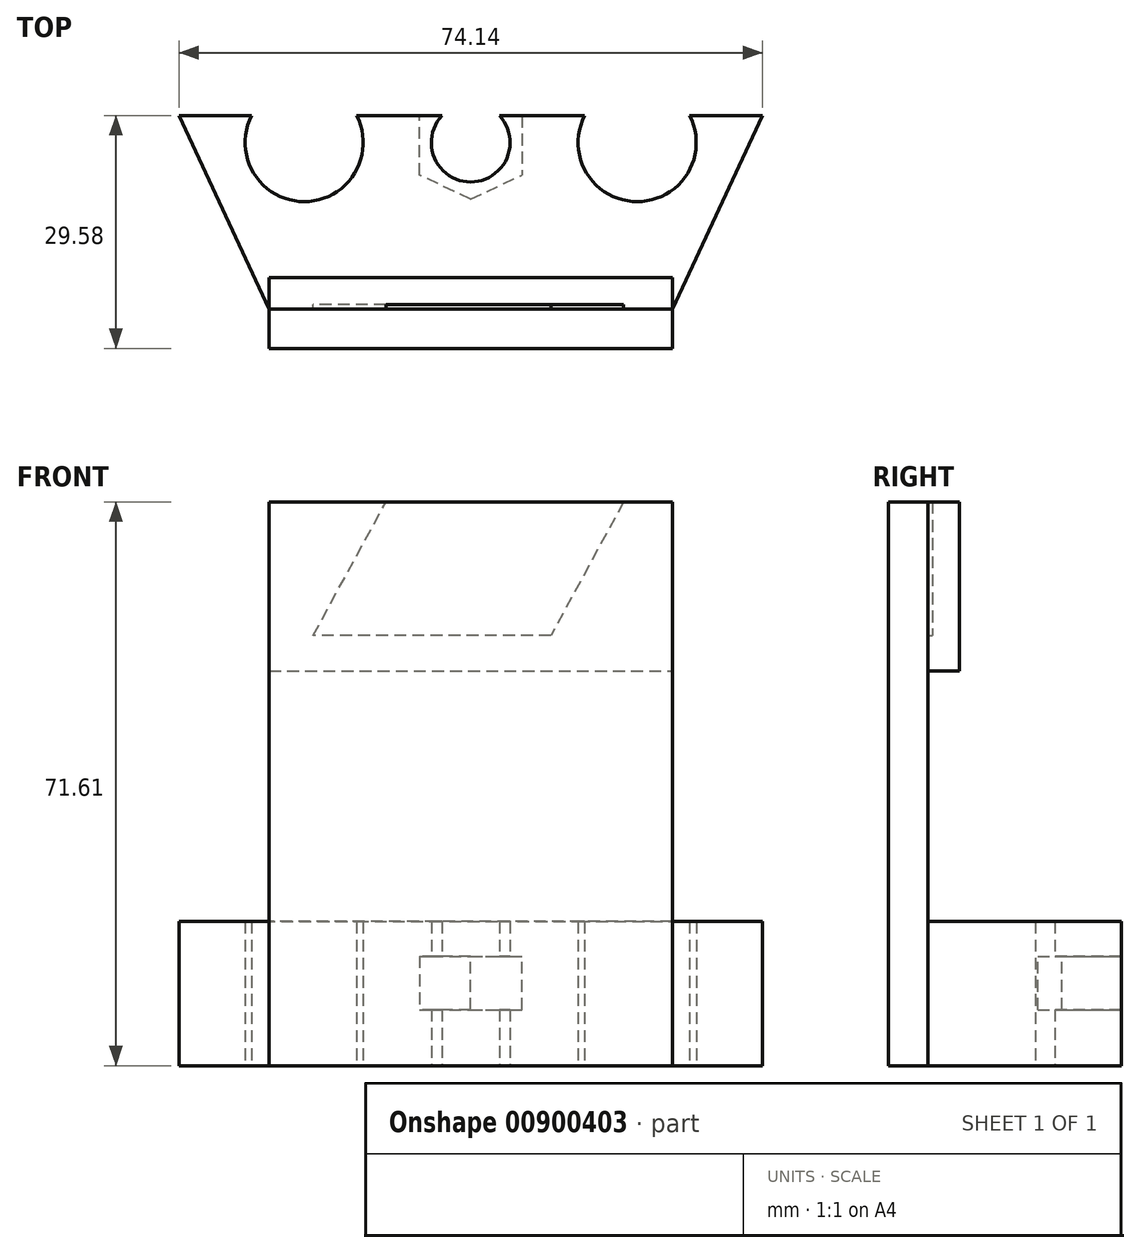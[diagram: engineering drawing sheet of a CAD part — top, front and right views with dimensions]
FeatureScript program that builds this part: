
annotation { "Feature Type Name" : "Feature", "Feature Type Description" : "" }
export const myFeature = defineFeature(function(context is Context, id is Id, definition is map)
    precondition{}
    {
        {
            var Q0;
            Q0=qCreatedBy(makeId("Top.planeOp"),FACE);
            var sketch = newSketch(context, id + "F0", { "sketchPlane" : qUnion([Q0])});
            skPoint(sketch, "E0.middle", {"position": v(0, 0) * mm});
            skCircle(sketch, "E1", {"center": v(21.15, 0) * mm, "radius": 7.5 * mm});
            skCircle(sketch, "E2", {"center": v(-21.15, 0) * mm, "radius": 7.5 * mm});
            skLineSegment(sketch, "E3", {"start": v(-6.5, 0) * mm, "end": v(-6.5, 4.12) * mm});
            skLineSegment(sketch, "E4", {"start": v(-6.5, 0) * mm, "end": v(-6.5, -4.12) * mm});
            skLineSegment(sketch, "E5", {"start": v(6.5, 0) * mm, "end": v(6.5, 4.12) * mm});
            skLineSegment(sketch, "E6", {"start": v(6.5, 0) * mm, "end": v(6.5, -4.12) * mm});
            skLineSegment(sketch, "E7", {"start": v(0, 7.2) * mm, "end": v(-6.5, 4.12) * mm});
            skLineSegment(sketch, "E8", {"start": v(0, 7.2) * mm, "end": v(6.5, 4.12) * mm});
            skLineSegment(sketch, "E9", {"start": v(0, -7.2) * mm, "end": v(-6.5, -4.12) * mm});
            skLineSegment(sketch, "E10", {"start": v(0, -7.2) * mm, "end": v(6.5, -4.12) * mm});
            skSolve(sketch);
        }
        {
            var Q0;
            Q0=makeQuery(id+"F0.imprint","IMPRINT",FACE,{"disambiguationData":[TD([[makeQuery(id+"F0.imprint","IMPRINT",EDGE,{"derivedFrom":sQuery(id+"F0.wireOp",EDGE,"E2")}),1.0]])]});
            var Q1;
            Q1=makeQuery(id+"F0.imprint","IMPRINT",FACE,{"disambiguationData":[TD([[makeQuery(id+"F0.imprint","IMPRINT",EDGE,{"derivedFrom":sQuery(id+"F0.wireOp",EDGE,"E1")}),1.0]])]});
            extrude(context, id + "F1", {"entities" : qUnion([Q0, Q1]), "depth" : 7.6 * mm, "offsetDistance" : 25 * mm, "hasSecondDirection" : true, "secondDirectionOppositeDirection" : true, "secondDirectionDepth" : 17.3 * mm});
        }
        {
            var Q0;
            Q0=makeQuery(id+"F0.imprint","IMPRINT",FACE,{"disambiguationData":[TD([[makeQuery(id+"F0.imprint","IMPRINT",EDGE,{"derivedFrom":sQuery(id+"F0.wireOp",EDGE,"E3")}),-1.0]])]});
            extrude(context, id + "F2", {"entities" : qUnion([Q0]), "oppositeDirection" : true, "depth" : 6.8 * mm, "offsetDistance" : 25 * mm});
        }
        {
            var Q0;
            Q0=qCreatedBy(makeId("Top.planeOp"),FACE);
            var sketch = newSketch(context, id + "F3", { "sketchPlane" : qUnion([Q0])});
            skLineSegment(sketch, "E11.top", {"start": v(25.61, -21.15) * mm, "end": v(-25.61, -21.15) * mm});
            skPoint(sketch, "E11.middle", {"position": v(0, 0) * mm});
            skLineSegment(sketch, "E12", {"start": v(-37.07, 3.43) * mm, "end": v(37.07, 3.43) * mm});
            skPoint(sketch, "E13.orphan", {"position": v(-53, 21.15) * mm});
            skPoint(sketch, "E14.orphan", {"position": v(53, 21.15) * mm});
            skLineSegment(sketch, "E15", {"start": v(-37.07, 3.43) * mm, "end": v(-25.61, -21.15) * mm});
            skLineSegment(sketch, "E16", {"start": v(37.07, 3.43) * mm, "end": v(25.61, -21.15) * mm});
            skPoint(sketch, "E17.orphan", {"position": v(-53, -21.15) * mm});
            skPoint(sketch, "E11.left.end.orphan", {"position": v(53, -21.15) * mm});
            skSolve(sketch);
        }
        {
            var Q0;
            Q0 = qSketchRegion(id + "F3", true);
            extrude(context, id + "F4", {"entities" : qUnion([Q0]), "depth" : 4.4 * mm, "offsetDistance" : 25 * mm, "hasSecondDirection" : true, "secondDirectionOppositeDirection" : true, "secondDirectionDepth" : 13.9 * mm});
        }
        {
            var Q0;
            Q0=makeQuery(id+"F1.opExtrude","SWEPT_BODY",BODY,{"disambiguationData":[OSD([sQuery(id+"F0.wireOp",EDGE,"E2")])]});
            var Q1;
            Q1=makeQuery(id+"F2.opExtrude","SWEPT_BODY",BODY,{"disambiguationData":[OSD([sQuery(id+"F0.wireOp",EDGE,"E3"),sQuery(id+"F0.wireOp",EDGE,"E4"),sQuery(id+"F0.wireOp",EDGE,"E5"),sQuery(id+"F0.wireOp",EDGE,"E6"),sQuery(id+"F0.wireOp",EDGE,"E7"),sQuery(id+"F0.wireOp",EDGE,"E8"),sQuery(id+"F0.wireOp",EDGE,"E9"),sQuery(id+"F0.wireOp",EDGE,"E10")])]});
            var Q2;
            Q2=makeQuery(id+"F1.opExtrude","SWEPT_BODY",BODY,{"disambiguationData":[OSD([sQuery(id+"F0.wireOp",EDGE,"E1")])]});
            var Q3;
            Q3=makeQuery(id+"F4.opExtrude","SWEPT_BODY",BODY,{"disambiguationData":[OSD([sQuery(id+"F3.wireOp",EDGE,"E11.top"),sQuery(id+"F3.wireOp",EDGE,"E12"),sQuery(id+"F3.wireOp",EDGE,"E15"),sQuery(id+"F3.wireOp",EDGE,"E16")])]});
            booleanBodies(context, id + "F5", {"operationType" : BooleanOperationType.SUBTRACTION, "tools" : qUnion([Q0, Q1, Q2]), "targets" : qUnion([Q3])});
        }
        {
            var Q0;
            Q0=makeQuery(id+"F4.opExtrude","SWEPT_FACE",FACE,{"disambiguationData":[OSD([sQuery(id+"F3.wireOp",EDGE,"E11.top")])]});
            var sketch = newSketch(context, id + "F6", { "sketchPlane" : qUnion([Q0])});
            skLineSegment(sketch, "E18.bottom", {"start": v(25.61, -13.9) * mm, "end": v(-25.61, -13.9) * mm});
            skLineSegment(sketch, "E18.top", {"start": v(25.61, 57.71) * mm, "end": v(-25.61, 57.71) * mm});
            skLineSegment(sketch, "E18.left", {"start": v(25.61, -13.9) * mm, "end": v(25.61, 57.71) * mm});
            skLineSegment(sketch, "E18.right", {"start": v(-25.61, -13.9) * mm, "end": v(-25.61, 57.71) * mm});
            skSolve(sketch);
        }
        {
            var Q0;
            Q0 = qSketchRegion(id + "F6", true);
            extrude(context, id + "F7", {"entities" : qUnion([Q0]), "operationType" : NewBodyOperationType.ADD, "depth" : 5 * mm, "offsetDistance" : 25 * mm});
        }
        {
            var Q0;
            Q0=makeQuery(id+"F7.opExtrude","CAP_FACE",FACE,{"disambiguationData":[OSD([sQuery(id+"F6.wireOp",EDGE,"E18.bottom"),sQuery(id+"F6.wireOp",EDGE,"E18.top"),sQuery(id+"F6.wireOp",EDGE,"E18.left"),sQuery(id+"F6.wireOp",EDGE,"E18.right")])],"isStart":true});
            cPlane(context, id + "F8", {"entities" : qUnion([Q0]), "cplaneType" : CPlaneType.OFFSET, "offset" : 0.6 * mm, "width" : 150 * mm, "height" : 150 * mm});
        }
        {
            var Q0;
            Q0=qCreatedBy(id+"F8.planeOp",FACE);
            var sketch = newSketch(context, id + "F9", { "sketchPlane" : qUnion([Q0])});
            skPoint(sketch, "E19.middle", {"position": v(15.52, 42.84) * mm});
            skLineSegment(sketch, "E20.bottom", {"start": v(-20, 40.77) * mm, "end": v(20, 40.77) * mm});
            skLineSegment(sketch, "E20.top", {"start": v(-20, 58.77) * mm, "end": v(20, 58.77) * mm});
            skLineSegment(sketch, "E20.left", {"start": v(-20, 40.77) * mm, "end": v(-20, 58.77) * mm});
            skLineSegment(sketch, "E20.right", {"start": v(20, 40.77) * mm, "end": v(20, 58.77) * mm});
            skPoint(sketch, "E20.middle", {"position": v(0, 49.77) * mm});
            skLineSegment(sketch, "E21", {"start": v(20, 40.77) * mm, "end": v(10.2, 58.77) * mm});
            skLineSegment(sketch, "E22", {"start": v(-20, 58.77) * mm, "end": v(-10.2, 40.77) * mm});
            skSolve(sketch);
        }
        {
            var Q0;
            {var subQ0=sQuery(id+"F9.wireOp",EDGE,"E21");Q0=makeQuery(id+"F9.imprint","IMPRINT",FACE,{"disambiguationData":[TD([[makeQuery(id+"F9.imprint","IMPRINT",EDGE,{"derivedFrom":subQ0}),1.0]])]});}
            extrude(context, id + "F10", {"entities" : qUnion([Q0]), "oppositeDirection" : true, "depth" : 0.6 * mm, "offsetDistance" : 25 * mm});
        }
        {
            var Q0;
            Q0=makeQuery(id+"F7.opExtrude","CAP_FACE",FACE,{"disambiguationData":[OSD([sQuery(id+"F6.wireOp",EDGE,"E18.bottom"),sQuery(id+"F6.wireOp",EDGE,"E18.top"),sQuery(id+"F6.wireOp",EDGE,"E18.left"),sQuery(id+"F6.wireOp",EDGE,"E18.right")])],"isStart":true});
            var sketch = newSketch(context, id + "F11", { "sketchPlane" : qUnion([Q0])});
            skLineSegment(sketch, "E23.bottom", {"start": v(25.61, 57.71) * mm, "end": v(-25.61, 57.71) * mm});
            skLineSegment(sketch, "E23.top", {"start": v(25.61, 36.27) * mm, "end": v(-25.61, 36.27) * mm});
            skLineSegment(sketch, "E23.left", {"start": v(25.61, 57.71) * mm, "end": v(25.61, 36.27) * mm});
            skLineSegment(sketch, "E23.right", {"start": v(-25.61, 57.71) * mm, "end": v(-25.61, 36.27) * mm});
            skSolve(sketch);
        }
        {
            var Q0;
            Q0 = qSketchRegion(id + "F11", true);
            extrude(context, id + "F12", {"entities" : qUnion([Q0]), "depth" : 4 * mm, "offsetDistance" : 25 * mm});
        }
        {
            var Q0;
            Q0=makeQuery(id+"F10.opExtrude","SWEPT_BODY",BODY,{"disambiguationData":[OSD([sQuery(id+"F9.wireOp",EDGE,"E20.bottom"),sQuery(id+"F9.wireOp",EDGE,"E20.top"),sQuery(id+"F9.wireOp",EDGE,"fwrjMXQo-WK6m-b8dY-bK3l-eFTgvQqSunGT"),sQuery(id+"F9.wireOp",EDGE,"8jJp1skS-lJIg-1qho-8Ot2-DPL0oGVGmFII")])]});
            var Q1;
            Q1=makeQuery(id+"F12.opExtrude","SWEPT_BODY",BODY,{"disambiguationData":[OSD([sQuery(id+"F11.wireOp",EDGE,"E23.bottom"),sQuery(id+"F11.wireOp",EDGE,"E23.top"),sQuery(id+"F11.wireOp",EDGE,"E23.left"),sQuery(id+"F11.wireOp",EDGE,"E23.right")])]});
            booleanBodies(context, id + "F13", {"operationType" : BooleanOperationType.SUBTRACTION, "tools" : qUnion([Q0]), "targets" : qUnion([Q1])});
        }
        {
            var Q0;
            Q0=makeQuery(id+"F7.boolean.opBoolean","MERGE",FACE,{"derivedFrom":[makeQuery(id+"F4.opExtrude","CAP_FACE",FACE,{"disambiguationData":[OSD([sQuery(id+"F3.wireOp",EDGE,"E11.top"),sQuery(id+"F3.wireOp",EDGE,"E12"),sQuery(id+"F3.wireOp",EDGE,"E15"),sQuery(id+"F3.wireOp",EDGE,"E16")])],"isStart":true}),makeQuery(id+"F7.opExtrude","SWEPT_FACE",FACE,{"disambiguationData":[OSD([sQuery(id+"F6.wireOp",EDGE,"E18.bottom")])]})]});
            var sketch = newSketch(context, id + "F14", { "sketchPlane" : qUnion([Q0])});
            skLineSegment(sketch, "E24.0.0", {"start": v(-6.5, -3.43) * mm, "end": v(-6.5, 4.12) * mm});
            skLineSegment(sketch, "E24.0.1", {"start": v(-6.5, 4.12) * mm, "end": v(0, 7.2) * mm});
            skLineSegment(sketch, "E24.0.2", {"start": v(0, 7.2) * mm, "end": v(6.5, 4.12) * mm});
            skLineSegment(sketch, "E24.0.3", {"start": v(6.5, 4.12) * mm, "end": v(6.5, -3.43) * mm});
            skLineSegment(sketch, "E24.0.4", {"start": v(6.5, -3.43) * mm, "end": v(-6.5, -3.43) * mm});
            skLineSegment(sketch, "E25.bottom", {"start": v(-6.5, 4.12) * mm, "end": v(6.5, 4.12) * mm});
            skLineSegment(sketch, "E25.top", {"start": v(-6.5, -12.92) * mm, "end": v(6.5, -12.92) * mm});
            skLineSegment(sketch, "E25.left", {"start": v(-6.5, 4.12) * mm, "end": v(-6.5, -12.92) * mm});
            skLineSegment(sketch, "E25.right", {"start": v(6.5, 4.12) * mm, "end": v(6.5, -12.92) * mm});
            skSolve(sketch);
        }
        {
            var Q0;
            {var subQ9=sQuery(id+"F14.wireOp",EDGE,"E24.0.1");Q0=makeQuery(id+"F14.imprint","IMPRINT",FACE,{"disambiguationData":[TD([[makeQuery(id+"F14.imprint","IMPRINT",EDGE,{"derivedFrom":subQ9}),1.0]])]});}
            var sketch = newSketch(context, id + "F15", { "sketchPlane" : qUnion([Q0])});
            skCircle(sketch, "E26", {"center": v(0, 0) * mm, "radius": 5 * mm});
            skSolve(sketch);
        }
        {
            var Q0;
            Q0 = qSketchRegion(id + "F15", true);
            extrude(context, id + "F16", {"entities" : qUnion([Q0]), "operationType" : NewBodyOperationType.REMOVE, "oppositeDirection" : true, "depth" : 25 * mm, "offsetDistance" : 25 * mm, "hasSecondDirection" : true, "secondDirectionOppositeDirection" : false, "secondDirectionDepth" : 25 * mm});
        }
    });
